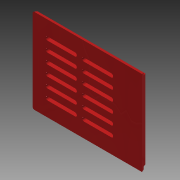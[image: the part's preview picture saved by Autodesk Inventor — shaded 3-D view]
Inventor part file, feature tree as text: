
AUTODESK INVENTOR PART (.ipt)
format: ipt  version: 2015 SP1 (Build 190203100, 203)  size: 537,600 bytes
history: native  units: mm
features: other x8, extrude x4, projected_geometry x2, loft x1, sketch x1
ambient origin geometry x8: Origin, YZ Plane, XZ Plane, XY Plane, X Axis, Y Axis, Z Axis, Center Point
bodies: Solid3 (feature_tree), Solid1 (feature_tree)
feature tree (16):
  other  "ESC Encl Bottom.ipt"
  other  "Bottom"
  other  "MidCleraance"
  other  "Mid"
  other  "Top"
  extrude  "Extrusion1"  TaperAngle=0.0deg  [1 undecoded]
  loft  "Loft3"
  extrude  "Extrusion4"  Depth=10.0mm
  other  "Lid Holes"
  extrude  "Extrusion3"  Depth=10.0mm TaperAngle=0.0deg
  extrude  "Extrusion5"  Depth=10.0mm
  other  "Solid2::ESC Encl Bottom.ipt"
  other  "TaggingFeature1"
  projected_geometry  "Projected Loop1"
  sketch  "Sketch7"  dims[d0=10.0mm d5=0.0mm d6=0.0mm d9=3.5mm d10=8.0mm d11=8.0mm d12=10.0mm d13=0.0mm d26=0.5mm d27=0.5mm d28=10.0mm d29=0.0mm d30=0.5mm d31=0.5mm d32=0.5mm d33=0.5mm d34=0.0mm d35=90.0deg d36=0.0mm d37=90.0deg d38=10.0mm d39=8.0mm d40=8.0mm d42=8.0mm d44=60.0mm d46=10.0mm d47=20.0mm d49=35.0mm d53=10.0mm d54=0.0mm d55=30.0mm]
  projected_geometry  "Project Cut Edges1"
note: 1 required parameter value undecoded (feature->parameter linkage not recoverable at this tier; creation-order binding heuristic only, values carry confidence <= 0.55)
